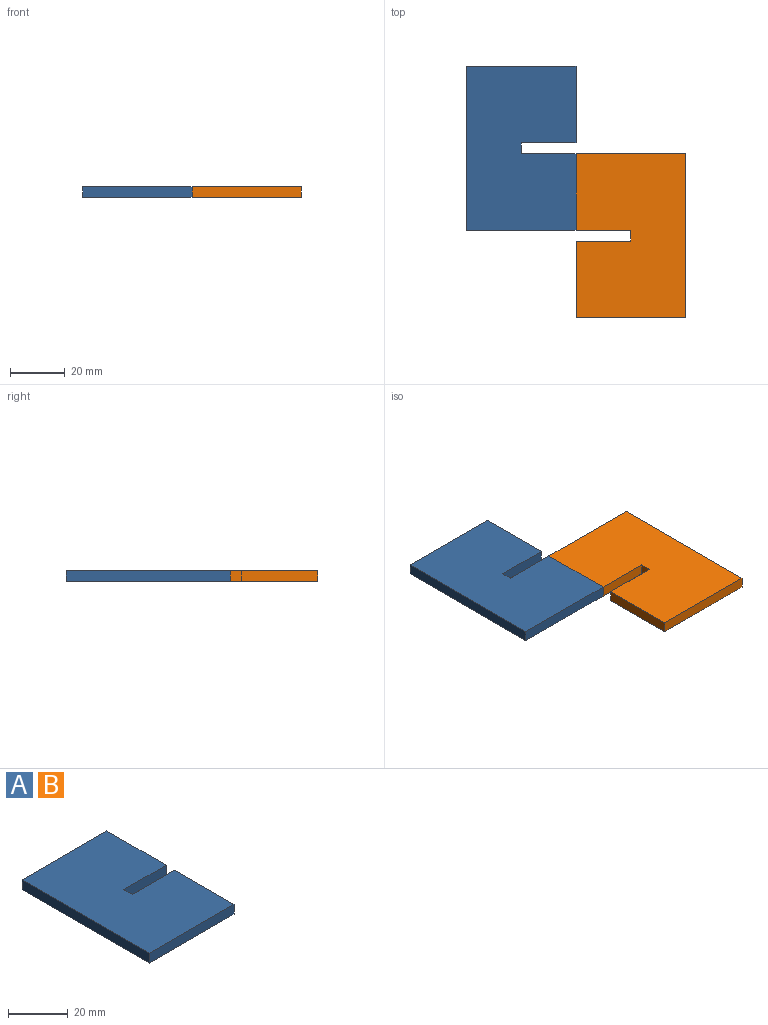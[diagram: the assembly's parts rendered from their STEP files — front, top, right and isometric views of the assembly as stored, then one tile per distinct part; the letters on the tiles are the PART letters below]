
ASSEMBLY  parts=2 mates=1
PART A: 10 faces, bbox 40x60x4 mm
  f0: plane 20x4mm, normal (0,-1,0), area 80mm2, adj f1,f7,f8,f9
  f1: plane 28x4mm, normal (1,0,0), area 112mm2, adj f0,f2,f8,f9
  f2: plane 40x4mm, normal (0,1,0), area 160mm2, adj f1,f3,f8,f9
  f3: plane 60x4mm, normal (-1,0,0), area 240mm2, adj f2,f4,f8,f9
  f4: plane 40x4mm, normal (0,-1,0), area 160mm2, adj f3,f5,f8,f9
  f5: plane 28x4mm, normal (1,0,0), area 112mm2, adj f4,f6,f8,f9
  f6: plane 20x4mm, normal (0,1,0), area 80mm2, adj f5,f7,f8,f9
  f7: plane 4x4mm, normal (1,0,0), area 16mm2, adj f0,f6,f8,f9
  f8: plane 60x40mm, normal (0,0,1), area 2320mm2, adj f0,f1,f2,f3,f4,f5,f6,f7
  f9: plane 60x40mm, normal (0,0,-1), area 2320mm2, adj f0,f1,f2,f3,f4,f5,f6,f7
PART B: same geometry as A
PLACE A t=(-2.48,-12.44,9.16)mm
PLACE B rot(axis=(0,1,0),180deg) t=(77.52,-44.44,13.16)mm
MATE fastened B.f1 <-> A.f5  axis (-1,0,0) through (37.52,1.56,11.16)mm
